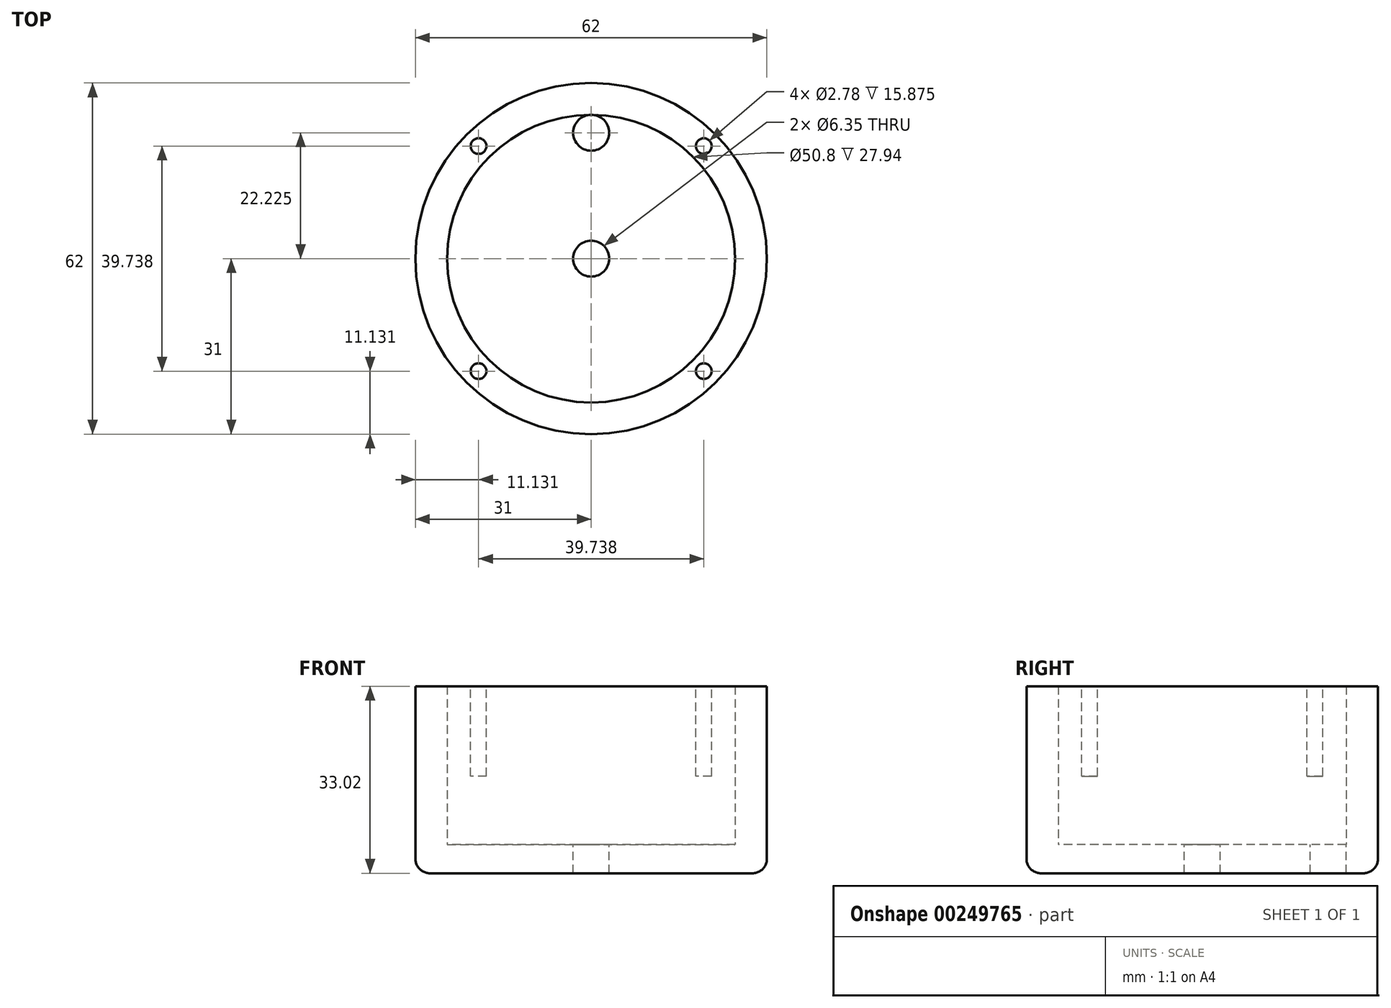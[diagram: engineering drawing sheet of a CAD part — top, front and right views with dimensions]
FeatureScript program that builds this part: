
annotation { "Feature Type Name" : "Feature", "Feature Type Description" : "" }
export const myFeature = defineFeature(function(context is Context, id is Id, definition is map)
    precondition{}
    {
        {
            var Q0;
            Q0=qCreatedBy(makeId("Top.planeOp"),FACE);
            var sketch = newSketch(context, id + "F0", { "sketchPlane" : qUnion([Q0])});
            skCircle(sketch, "E0", {"center": v(0, 0) * mm, "radius": 31 * mm});
            skCircle(sketch, "E1", {"center": v(0, 0) * mm, "radius": 25.4 * mm});
            skCircle(sketch, "E2", {"center": v(0, 0) * mm, "radius": 28.1 * mm, "construction": true});
            skLineSegment(sketch, "E3", {"start": v(0, 0) * mm, "end": v(-31, 0) * mm, "construction": true});
            skLineSegment(sketch, "E4", {"start": v(0, 0) * mm, "end": v(-21.92, 21.92) * mm, "construction": true});
            skSolve(sketch);
        }
        {
            var Q0;
            Q0 = qSketchRegion(id + "F0", true);
            extrude(context, id + "F1", {"entities" : qUnion([Q0]), "depth" : 27.94 * mm});
        }
        {
            var Q0;
            Q0=makeQuery(id+"F1.opExtrude","CAP_FACE",FACE,{"disambiguationData":[OSD([sQuery(id+"F0.wireOp",EDGE,"E0"),sQuery(id+"F0.wireOp",EDGE,"E1")])],"isStart":true});
            var sketch = newSketch(context, id + "F2", { "sketchPlane" : qUnion([Q0])});
            skCircle(sketch, "E5", {"center": v(0, 0) * mm, "radius": 31 * mm});
            skCircle(sketch, "E6", {"center": v(0, 0) * mm, "radius": 3.18 * mm});
            skCircle(sketch, "E7", {"center": v(0, -22.23) * mm, "radius": 3.18 * mm});
            skSolve(sketch);
        }
        {
            var Q0;
            Q0 = qSketchRegion(id + "F2", true);
            extrude(context, id + "F3", {"entities" : qUnion([Q0]), "operationType" : NewBodyOperationType.ADD, "depth" : 5.08 * mm});
        }
        {
            var Q0;
            Q0=makeQuery(id+"F1.opExtrude","CAP_EDGE",EDGE,{"disambiguationData":[OSD([sQuery(id+"F0.wireOp",EDGE,"E1")])],"isStart":true});
            var Q1;
            Q1=makeQuery(id+"F3.opExtrude","CAP_EDGE",EDGE,{"disambiguationData":[OSD([sQuery(id+"F2.wireOp",EDGE,"E5")])],"isStart":false});
            fillet(context, id + "F4", {"entities" : qUnion([Q0, Q1]), "radius" : 2.54 * mm, "tangentPropagation" : true, "allowEdgeOverflow" : false});
        }
        {
            var Q0;
            Q0=makeQuery(id+"F1.opExtrude","CAP_FACE",FACE,{"disambiguationData":[OSD([sQuery(id+"F0.wireOp",EDGE,"E0"),sQuery(id+"F0.wireOp",EDGE,"E1")])],"isStart":false});
            var sketch = newSketch(context, id + "F5", { "sketchPlane" : qUnion([Q0])});
            skCircle(sketch, "E8", {"center": v(0, 0) * mm, "radius": 28.1 * mm, "construction": true});
            skLineSegment(sketch, "E9", {"start": v(0, 0) * mm, "end": v(0, 28.1) * mm, "construction": true});
            skLineSegment(sketch, "E10", {"start": v(0, 0) * mm, "end": v(-19.87, 19.87) * mm, "construction": true});
            skCircle(sketch, "E11", {"center": v(-19.87, 19.87) * mm, "radius": 1.39 * mm});
            skCircle(sketch, "E12.1.0", {"center": v(-19.87, -19.87) * mm, "radius": 1.39 * mm});
            skCircle(sketch, "E12.2.0", {"center": v(19.87, -19.87) * mm, "radius": 1.39 * mm});
            skCircle(sketch, "E12.3.0", {"center": v(19.87, 19.87) * mm, "radius": 1.39 * mm});
            skSolve(sketch);
        }
        {
            var Q0;
            Q0 = qSketchRegion(id + "F5", true);
            extrude(context, id + "F6", {"entities" : qUnion([Q0]), "operationType" : NewBodyOperationType.REMOVE, "oppositeDirection" : true, "depth" : 15.88 * mm});
        }
    });
